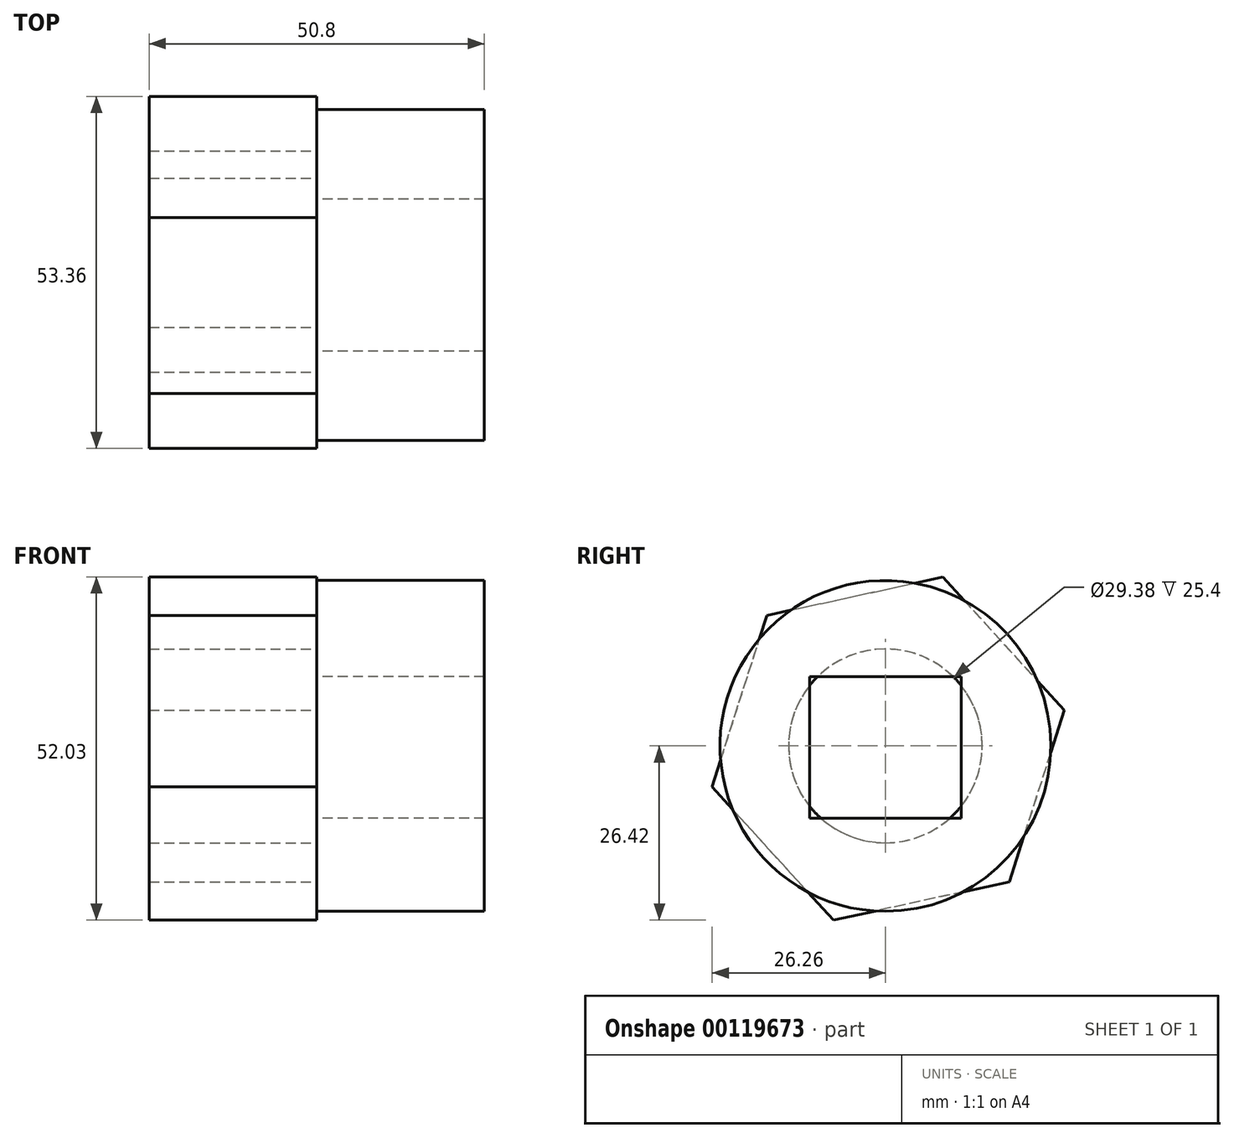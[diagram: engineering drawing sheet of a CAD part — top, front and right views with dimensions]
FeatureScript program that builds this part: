
annotation { "Feature Type Name" : "Feature", "Feature Type Description" : "" }
export const myFeature = defineFeature(function(context is Context, id is Id, definition is map)
    precondition{}
    {
        {
            var Q0;
            Q0=qCreatedBy(makeId("Right.planeOp"),FACE);
            var sketch = newSketch(context, id + "F0", { "sketchPlane" : qUnion([Q0])});
            skCircle(sketch, "E0", {"center": v(0, 0) * mm, "radius": 25.08 * mm});
            skCircle(sketch, "E1", {"center": v(0, 0) * mm, "radius": 38.2 * mm});
            skLineSegment(sketch, "E2.bottom", {"start": v(11.51, 10.5) * mm, "end": v(-11.51, 10.5) * mm});
            skLineSegment(sketch, "E2.top", {"start": v(11.51, -10.95) * mm, "end": v(-11.51, -10.95) * mm});
            skLineSegment(sketch, "E2.left", {"start": v(11.51, 10.5) * mm, "end": v(11.51, -10.95) * mm});
            skLineSegment(sketch, "E2.right", {"start": v(-11.51, 10.5) * mm, "end": v(-11.51, -10.95) * mm});
            skSolve(sketch);
        }
        {
            var Q0;
            Q0=makeQuery(id+"F0.imprint","IMPRINT",FACE,{"disambiguationData":[TD([[makeQuery(id+"F0.imprint","IMPRINT",EDGE,{"derivedFrom":sQuery(id+"F0.wireOp",EDGE,"E0")}),1.0]])]});
            extrude(context, id + "F1", {"entities" : qUnion([Q0]), "depth" : 25.4 * mm});
        }
        {
            var Q0;
            Q0=qCreatedBy(makeId("Right.planeOp"),FACE);
            var sketch = newSketch(context, id + "F2", { "sketchPlane" : qUnion([Q0])});
            skCircle(sketch, "E3.cCircle", {"center": v(0.42, -0.4) * mm, "radius": 23.65 * mm, "construction": true});
            skLineSegment(sketch, "E3.0", {"start": v(-17.96, 19.8) * mm, "end": v(8.72, 25.61) * mm});
            skLineSegment(sketch, "E3.1", {"start": v(8.72, 25.61) * mm, "end": v(27.1, 5.41) * mm});
            skLineSegment(sketch, "E3.2", {"start": v(27.1, 5.41) * mm, "end": v(18.8, -20.6) * mm});
            skLineSegment(sketch, "E3.3", {"start": v(18.8, -20.6) * mm, "end": v(-7.89, -26.42) * mm});
            skLineSegment(sketch, "E3.4", {"start": v(-7.89, -26.42) * mm, "end": v(-26.26, -6.22) * mm});
            skLineSegment(sketch, "E3.5", {"start": v(-26.26, -6.22) * mm, "end": v(-17.96, 19.8) * mm});
            skPoint(sketch, "E3.0.midPoint", {"position": v(-4.62, 22.7) * mm});
            skCircle(sketch, "E4", {"center": v(0, 0) * mm, "radius": 14.69 * mm});
            skSolve(sketch);
        }
        {
            var Q0;
            Q0=makeQuery(id+"F2.imprint","IMPRINT",FACE,{"disambiguationData":[TD([[makeQuery(id+"F2.imprint","IMPRINT",EDGE,{"derivedFrom":sQuery(id+"F2.wireOp",EDGE,"E3.0")}),-1.0]])]});
            extrude(context, id + "F3", {"entities" : qUnion([Q0]), "operationType" : NewBodyOperationType.ADD, "oppositeDirection" : true, "depth" : 25.4 * mm});
        }
    });
